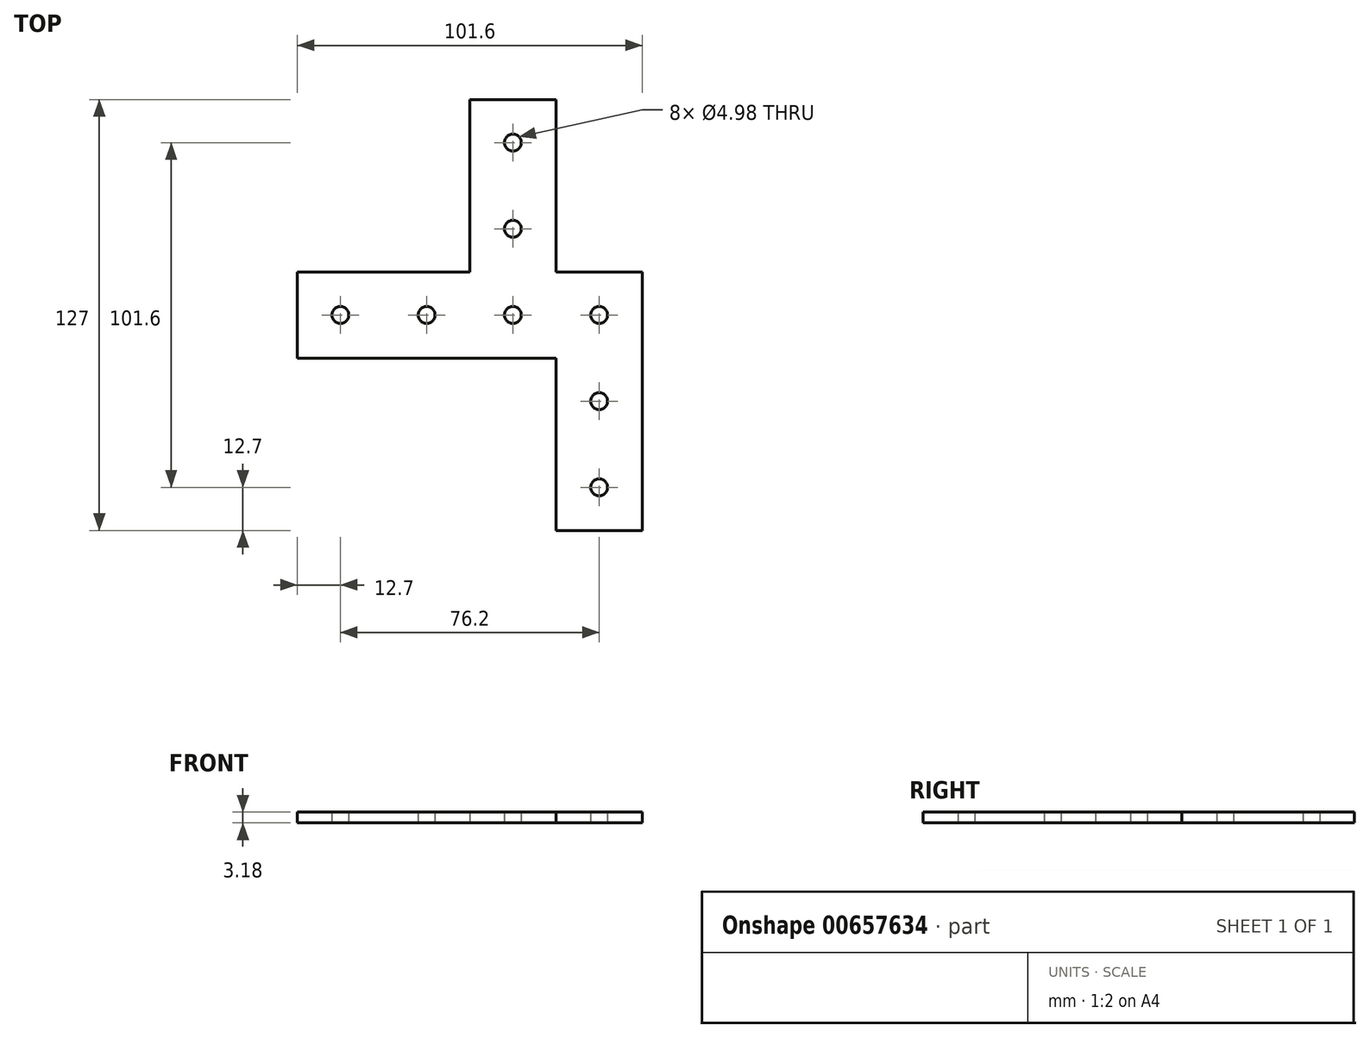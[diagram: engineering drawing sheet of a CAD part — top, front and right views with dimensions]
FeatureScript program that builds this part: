
annotation { "Feature Type Name" : "Feature", "Feature Type Description" : "" }
export const myFeature = defineFeature(function(context is Context, id is Id, definition is map)
    precondition{}
    {
        {
            var Q0;
            Q0=qCreatedBy(makeId("Top.planeOp"),FACE);
            var sketch = newSketch(context, id + "F0", { "sketchPlane" : qUnion([Q0])});
            skCircle(sketch, "E0", {"center": v(0, 0) * mm, "radius": 2.49 * mm});
            skCircle(sketch, "E1.0.1.0", {"center": v(0, 25.4) * mm, "radius": 2.49 * mm});
            skCircle(sketch, "E1.0.2.0", {"center": v(0, 50.8) * mm, "radius": 2.49 * mm});
            skLineSegment(sketch, "E1.direction1", {"start": v(0, 0) * mm, "end": v(25.4, 0) * mm, "construction": true});
            skLineSegment(sketch, "E1.direction2", {"start": v(0, 0) * mm, "end": v(0, 25.4) * mm, "construction": true});
            skCircle(sketch, "E2.1.0.0", {"center": v(-25.4, 50.8) * mm, "radius": 2.49 * mm});
            skCircle(sketch, "E2.2.0.0", {"center": v(-50.8, 50.8) * mm, "radius": 2.49 * mm});
            skCircle(sketch, "E2.3.0.0", {"center": v(-76.2, 50.8) * mm, "radius": 2.49 * mm});
            skLineSegment(sketch, "E2.direction1", {"start": v(0, 50.8) * mm, "end": v(-25.4, 50.8) * mm, "construction": true});
            skCircle(sketch, "E3.0.1.0", {"center": v(-25.4, 76.2) * mm, "radius": 2.49 * mm});
            skCircle(sketch, "E3.0.2.0", {"center": v(-25.4, 101.6) * mm, "radius": 2.49 * mm});
            skLineSegment(sketch, "E3.direction1", {"start": v(-25.4, 50.8) * mm, "end": v(0, 50.8) * mm, "construction": true});
            skLineSegment(sketch, "E3.direction2", {"start": v(-25.4, 50.8) * mm, "end": v(-25.4, 76.2) * mm, "construction": true});
            skLineSegment(sketch, "E4", {"start": v(-88.9, 38.1) * mm, "end": v(-88.9, 63.5) * mm});
            skLineSegment(sketch, "E5", {"start": v(-88.9, 63.5) * mm, "end": v(-38.1, 63.5) * mm});
            skLineSegment(sketch, "E6", {"start": v(-38.1, 63.5) * mm, "end": v(-38.1, 114.3) * mm});
            skLineSegment(sketch, "E7", {"start": v(-38.1, 114.3) * mm, "end": v(-12.7, 114.3) * mm});
            skLineSegment(sketch, "E8", {"start": v(-12.7, 114.3) * mm, "end": v(-12.7, 63.5) * mm});
            skLineSegment(sketch, "E9", {"start": v(-12.7, 63.5) * mm, "end": v(12.7, 63.5) * mm});
            skLineSegment(sketch, "E10", {"start": v(12.7, 63.5) * mm, "end": v(12.7, -12.7) * mm});
            skLineSegment(sketch, "E11", {"start": v(12.7, -12.7) * mm, "end": v(-12.7, -12.7) * mm});
            skLineSegment(sketch, "E12", {"start": v(-12.7, -12.7) * mm, "end": v(-12.7, 38.1) * mm});
            skLineSegment(sketch, "E13", {"start": v(-12.7, 38.1) * mm, "end": v(-88.9, 38.1) * mm});
            skSolve(sketch);
        }
        {
            var Q0;
            Q0=makeQuery(id+"F0.imprint","IMPRINT",FACE,{"disambiguationData":[TD([[makeQuery(id+"F0.imprint","IMPRINT",EDGE,{"derivedFrom":sQuery(id+"F0.wireOp",EDGE,"E0")}),-1.0]])]});
            extrude(context, id + "F1", {"entities" : qUnion([Q0]), "depth" : 3.17 * mm, "offsetDistance" : 25.4 * mm});
        }
    });
